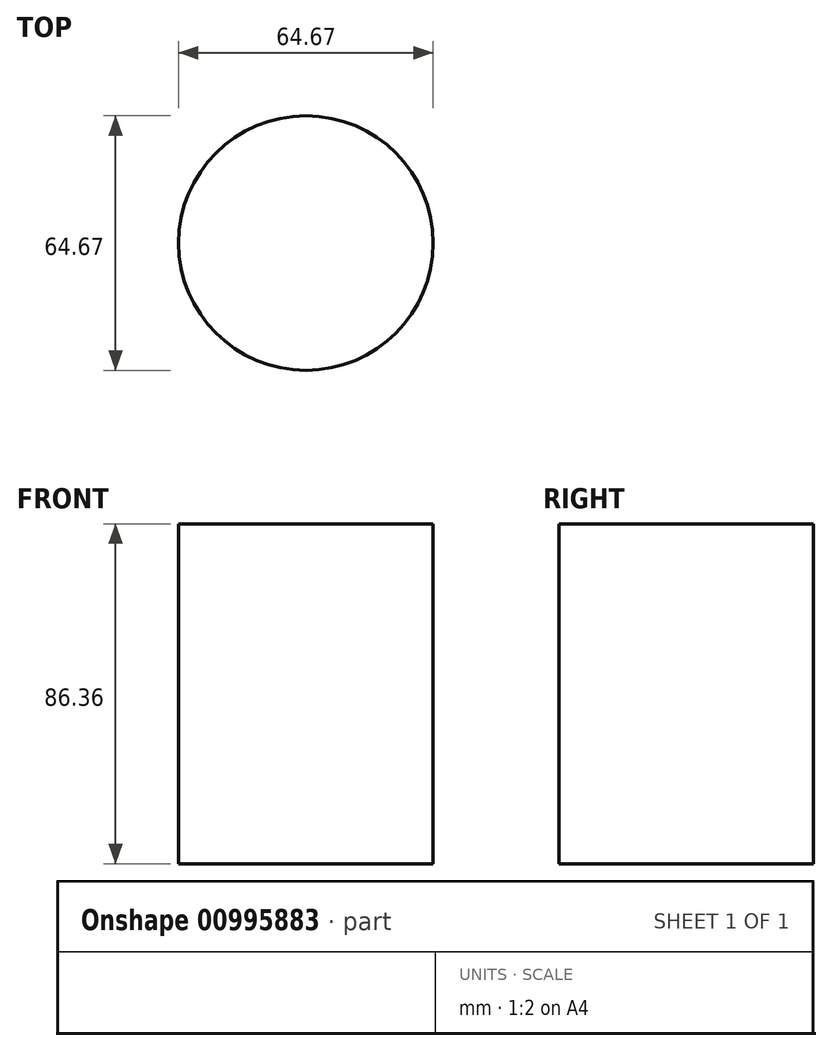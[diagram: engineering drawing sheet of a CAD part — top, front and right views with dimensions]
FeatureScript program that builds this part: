
annotation { "Feature Type Name" : "Feature", "Feature Type Description" : "" }
export const myFeature = defineFeature(function(context is Context, id is Id, definition is map)
    precondition{}
    {
        {
            var Q0;
            Q0=qCreatedBy(makeId("Top.planeOp"),FACE);
            var sketch = newSketch(context, id + "F0", { "sketchPlane" : qUnion([Q0])});
            skCircle(sketch, "E0", {"center": v(-41.92, -14.88) * mm, "radius": 32.34 * mm});
            skSolve(sketch);
        }
        {
            var Q0;
            Q0 = qSketchRegion(id + "F0", true);
            extrude(context, id + "F1", {"entities" : qUnion([Q0]), "depth" : 86.36 * mm, "offsetDistance" : 25.4 * mm});
        }
    });
